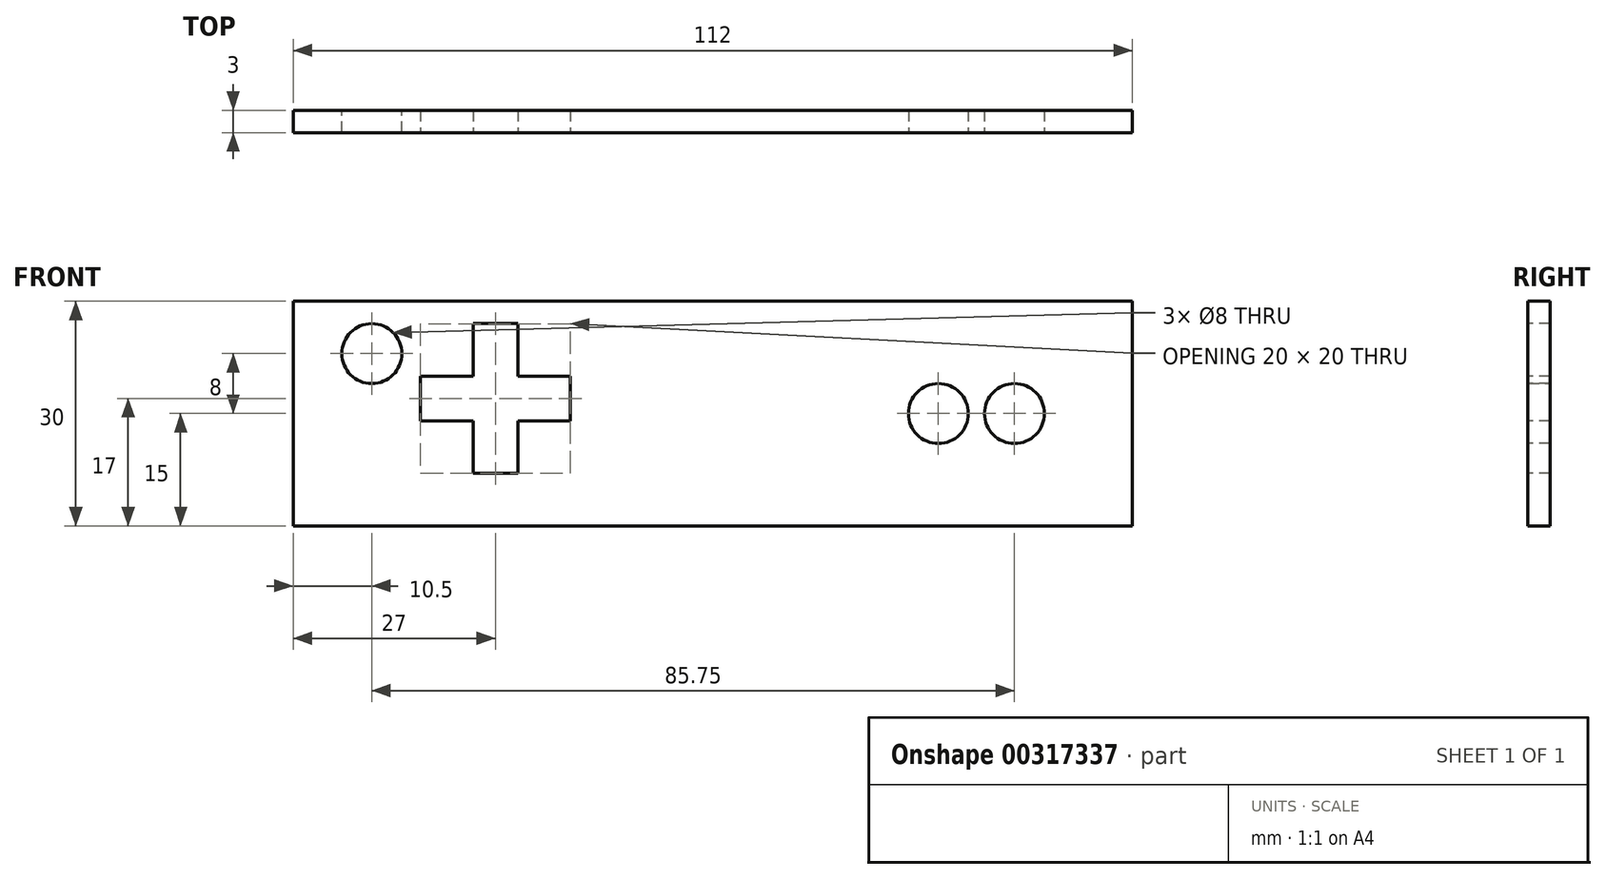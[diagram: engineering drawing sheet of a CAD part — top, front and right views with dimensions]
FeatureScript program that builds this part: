
annotation { "Feature Type Name" : "Feature", "Feature Type Description" : "" }
export const myFeature = defineFeature(function(context is Context, id is Id, definition is map)
    precondition{}
    {
        {
            var Q0;
            Q0=qCreatedBy(makeId("Front.planeOp"),FACE);
            var sketch = newSketch(context, id + "F0", { "sketchPlane" : qUnion([Q0])});
            skLineSegment(sketch, "E0.bottom", {"start": v(56, 15) * mm, "end": v(-56, 15) * mm});
            skLineSegment(sketch, "E0.top", {"start": v(56, -15) * mm, "end": v(-56, -15) * mm});
            skLineSegment(sketch, "E0.left", {"start": v(56, 15) * mm, "end": v(56, -15) * mm});
            skLineSegment(sketch, "E0.right", {"start": v(-56, 15) * mm, "end": v(-56, -15) * mm});
            skPoint(sketch, "E0.middle", {"position": v(0, 0) * mm});
            skLineSegment(sketch, "E1", {"start": v(-56, 15) * mm, "end": v(-56, 8) * mm, "construction": true});
            skLineSegment(sketch, "E2", {"start": v(-56, 8) * mm, "end": v(-45.5, 8) * mm, "construction": true});
            skCircle(sketch, "E3", {"center": v(-45.5, 8) * mm, "radius": 4 * mm});
            skSolve(sketch);
        }
        {
            var Q0;
            Q0 = qSketchRegion(id + "F0", true);
            extrude(context, id + "F1", {"entities" : qUnion([Q0]), "depth" : 3 * mm});
        }
        {
            var Q0;
            Q0=makeQuery(id+"F1.opExtrude","CAP_FACE",FACE,{"disambiguationData":[OSD([sQuery(id+"F0.wireOp",EDGE,"E0.bottom"),sQuery(id+"F0.wireOp",EDGE,"E0.top"),sQuery(id+"F0.wireOp",EDGE,"E0.left"),sQuery(id+"F0.wireOp",EDGE,"E0.right"),sQuery(id+"F0.wireOp",EDGE,"E3")])],"isStart":false});
            var sketch = newSketch(context, id + "F2", { "sketchPlane" : qUnion([Q0])});
            skLineSegment(sketch, "E4", {"start": v(-56, 15) * mm, "end": v(-29, 15) * mm, "construction": true});
            skLineSegment(sketch, "E5", {"start": v(-29, 15) * mm, "end": v(-29, 8) * mm, "construction": true});
            skLineSegment(sketch, "E6", {"start": v(-29, 8) * mm, "end": v(-29, -4) * mm, "construction": true});
            skLineSegment(sketch, "E7", {"start": v(-29, 2) * mm, "end": v(-35, 2) * mm, "construction": true});
            skPoint(sketch, "E7.endSnap0", {"position": v(-29, 2) * mm});
            skLineSegment(sketch, "E8", {"start": v(-29, 2) * mm, "end": v(-23, 2) * mm, "construction": true});
            skLineSegment(sketch, "E9", {"start": v(-35, 2) * mm, "end": v(-39, 2) * mm, "construction": true});
            skLineSegment(sketch, "E10", {"start": v(-39, 2) * mm, "end": v(-39, 5) * mm});
            skLineSegment(sketch, "E11.MirrorCS", {"start": v(-39, 2) * mm, "end": v(-39, -1) * mm});
            skLineSegment(sketch, "E12", {"start": v(-29, -4) * mm, "end": v(-29, -8) * mm, "construction": true});
            skLineSegment(sketch, "E13", {"start": v(-29, -8) * mm, "end": v(-32, -8) * mm});
            skLineSegment(sketch, "E14.MirrorCS", {"start": v(-29, -8) * mm, "end": v(-26, -8) * mm});
            skLineSegment(sketch, "E15.MirrorCS", {"start": v(-19, 2) * mm, "end": v(-19, 5) * mm});
            skLineSegment(sketch, "E16.MirrorCS", {"start": v(-19, 2) * mm, "end": v(-19, -1) * mm});
            skLineSegment(sketch, "E17", {"start": v(-39, -1) * mm, "end": v(-32, -1) * mm});
            skLineSegment(sketch, "E18", {"start": v(-32, -1) * mm, "end": v(-32, -8) * mm});
            skLineSegment(sketch, "E19", {"start": v(-26, -8) * mm, "end": v(-26, -1) * mm});
            skLineSegment(sketch, "E20", {"start": v(-26, -1) * mm, "end": v(-19, -1) * mm});
            skLineSegment(sketch, "E21.MirrorCS", {"start": v(-39, 5) * mm, "end": v(-32, 5) * mm});
            skLineSegment(sketch, "E22.MirrorCS", {"start": v(-32, 5) * mm, "end": v(-32, 12) * mm});
            skLineSegment(sketch, "E23.MirrorCS", {"start": v(-26, 12) * mm, "end": v(-26, 5) * mm});
            skLineSegment(sketch, "E24.MirrorCS", {"start": v(-29, 12) * mm, "end": v(-26, 12) * mm});
            skLineSegment(sketch, "E25.MirrorCS", {"start": v(-29, 12) * mm, "end": v(-32, 12) * mm});
            skLineSegment(sketch, "E26.MirrorCS", {"start": v(-26, 5) * mm, "end": v(-19, 5) * mm});
            skSolve(sketch);
        }
        {
            var Q0;
            Q0 = qSketchRegion(id + "F2", true);
            extrude(context, id + "F3", {"entities" : qUnion([Q0]), "operationType" : NewBodyOperationType.REMOVE, "oppositeDirection" : true, "depth" : 25 * mm});
        }
        {
            var Q0;
            Q0=makeQuery(id+"F1.opExtrude","CAP_FACE",FACE,{"disambiguationData":[OSD([sQuery(id+"F0.wireOp",EDGE,"E0.bottom"),sQuery(id+"F0.wireOp",EDGE,"E0.top"),sQuery(id+"F0.wireOp",EDGE,"E0.left"),sQuery(id+"F0.wireOp",EDGE,"E0.right"),sQuery(id+"F0.wireOp",EDGE,"E3")])],"isStart":false});
            var sketch = newSketch(context, id + "F4", { "sketchPlane" : qUnion([Q0])});
            skLineSegment(sketch, "E27", {"start": v(56, 15) * mm, "end": v(40.25, 15) * mm, "construction": true});
            skLineSegment(sketch, "E28", {"start": v(40.25, 15) * mm, "end": v(40.25, 0) * mm, "construction": true});
            skLineSegment(sketch, "E29", {"start": v(40.25, 0) * mm, "end": v(30.1, 0) * mm});
            skCircle(sketch, "E30", {"center": v(40.25, 0) * mm, "radius": 4 * mm});
            skCircle(sketch, "E31", {"center": v(30.1, 0) * mm, "radius": 4 * mm});
            skSolve(sketch);
        }
        {
            var Q0;
            Q0 = qSketchRegion(id + "F4", true);
            extrude(context, id + "F5", {"entities" : qUnion([Q0]), "operationType" : NewBodyOperationType.REMOVE, "oppositeDirection" : true, "depth" : 25 * mm});
        }
    });
